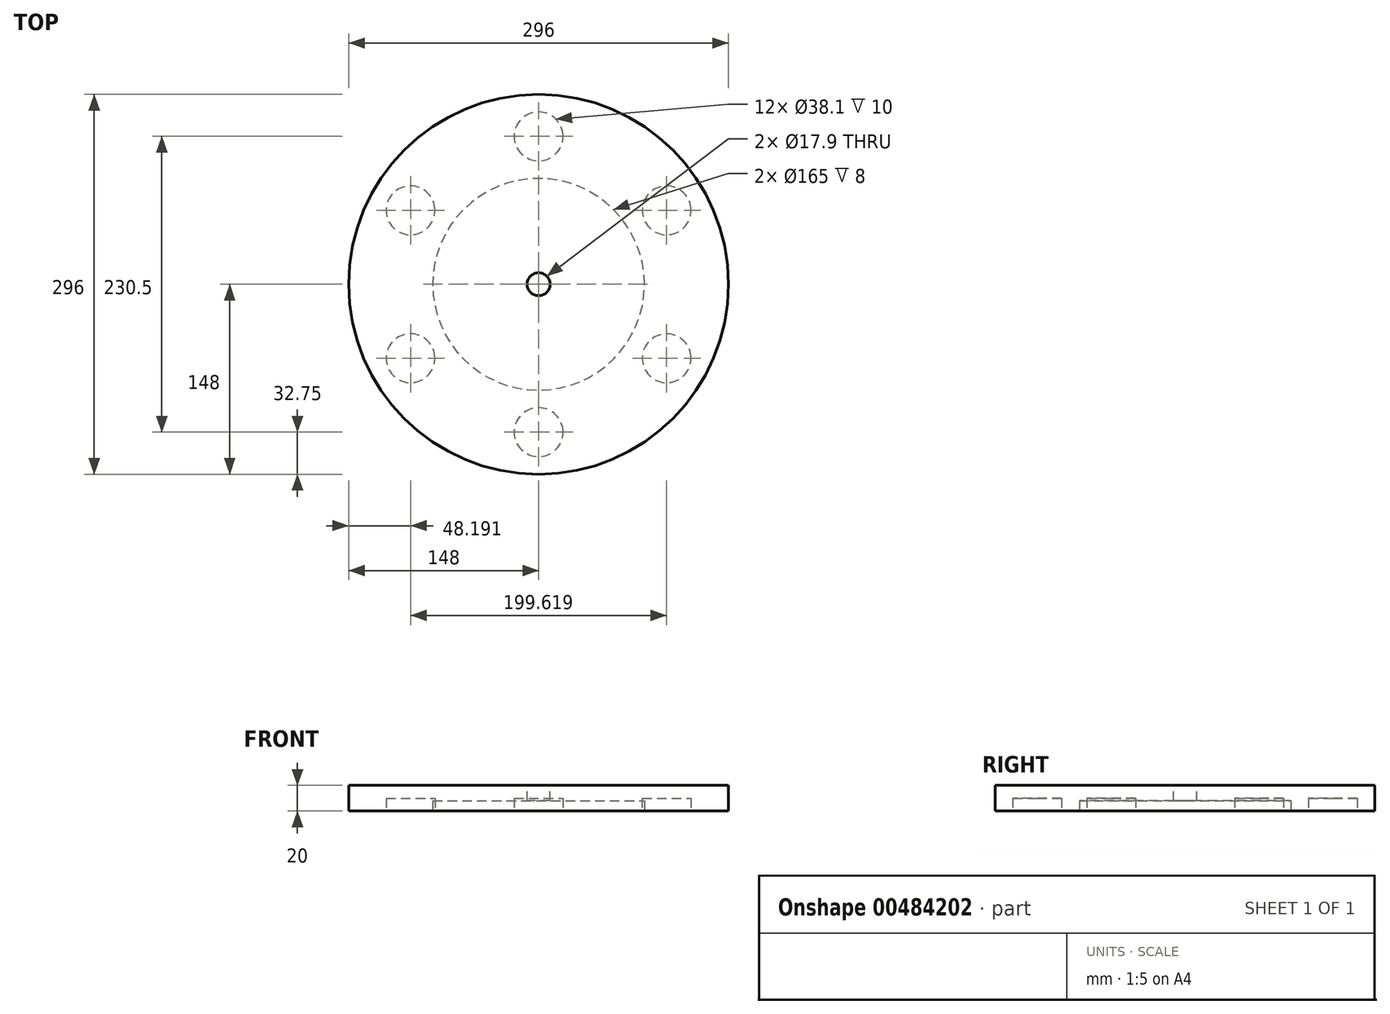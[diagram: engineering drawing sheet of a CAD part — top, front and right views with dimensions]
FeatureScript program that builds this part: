
annotation { "Feature Type Name" : "Feature", "Feature Type Description" : "" }
export const myFeature = defineFeature(function(context is Context, id is Id, definition is map)
    precondition{}
    {
        {
            var Q0;
            Q0=qCreatedBy(makeId("Top.planeOp"),FACE);
            var sketch = newSketch(context, id + "F0", { "sketchPlane" : qUnion([Q0])});
            skCircle(sketch, "E0", {"center": v(0, 0) * mm, "radius": 148 * mm});
            skCircle(sketch, "E1", {"center": v(0, 0) * mm, "radius": 8.95 * mm});
            skSolve(sketch);
        }
        {
            var Q0;
            Q0=makeQuery(id+"F0.imprint","IMPRINT",FACE,{"disambiguationData":[TD([[makeQuery(id+"F0.imprint","IMPRINT",EDGE,{"derivedFrom":sQuery(id+"F0.wireOp",EDGE,"E0")}),1.0]])]});
            extrude(context, id + "F1", {"entities" : qUnion([Q0]), "oppositeDirection" : true, "depth" : 20 * mm});
        }
        {
            var Q0;
            Q0=makeQuery(id+"F1.opExtrude","CAP_FACE",FACE,{"disambiguationData":[OSD([sQuery(id+"F0.wireOp",EDGE,"E0"),sQuery(id+"F0.wireOp",EDGE,"E1")])],"isStart":false});
            var sketch = newSketch(context, id + "F2", { "sketchPlane" : qUnion([Q0])});
            skCircle(sketch, "E2", {"center": v(0, 0) * mm, "radius": 82.5 * mm});
            skLineSegment(sketch, "E3", {"start": v(-82.5, 0) * mm, "end": v(-115.25, 0) * mm, "construction": true});
            skLineSegment(sketch, "E4", {"start": v(82.5, 0) * mm, "end": v(115.25, 0) * mm, "construction": true});
            skCircle(sketch, "E5", {"center": v(0, 0) * mm, "radius": 115.25 * mm, "construction": true});
            skLineSegment(sketch, "E6", {"start": v(0, 0) * mm, "end": v(0, 115.25) * mm, "construction": true});
            skLineSegment(sketch, "E7", {"start": v(0, 0) * mm, "end": v(99.8, 57.63) * mm, "construction": true});
            skLineSegment(sketch, "E8", {"start": v(0, 0) * mm, "end": v(99.8, -57.63) * mm, "construction": true});
            skLineSegment(sketch, "E9", {"start": v(0, 0) * mm, "end": v(0, -115.25) * mm, "construction": true});
            skLineSegment(sketch, "E10", {"start": v(0, 0) * mm, "end": v(-99.8, -57.63) * mm, "construction": true});
            skLineSegment(sketch, "E11", {"start": v(0, 0) * mm, "end": v(-99.8, 57.62) * mm, "construction": true});
            skCircle(sketch, "E12", {"center": v(-99.8, -57.63) * mm, "radius": 19.05 * mm});
            skCircle(sketch, "E13", {"center": v(0, -115.25) * mm, "radius": 19.05 * mm});
            skCircle(sketch, "E14", {"center": v(99.8, -57.62) * mm, "radius": 19.05 * mm});
            skCircle(sketch, "E15", {"center": v(99.8, 57.63) * mm, "radius": 19.05 * mm});
            skCircle(sketch, "E16", {"center": v(0, 115.25) * mm, "radius": 19.05 * mm});
            skCircle(sketch, "E17", {"center": v(-99.8, 57.62) * mm, "radius": 19.05 * mm});
            skSolve(sketch);
        }
        {
            var Q0;
            Q0=makeQuery(id+"F2.imprint","IMPRINT",FACE,{"disambiguationData":[TD([[makeQuery(id+"F2.imprint","IMPRINT",EDGE,{"derivedFrom":sQuery(id+"F2.wireOp",EDGE,"E2")}),1.0]])]});
            extrude(context, id + "F3", {"entities" : qUnion([Q0]), "operationType" : NewBodyOperationType.REMOVE, "oppositeDirection" : true, "depth" : 8 * mm});
        }
        {
            var Q0;
            Q0=makeQuery(id+"F2.imprint","IMPRINT",FACE,{"disambiguationData":[TD([[makeQuery(id+"F2.imprint","IMPRINT",EDGE,{"derivedFrom":sQuery(id+"F2.wireOp",EDGE,"E17")}),1.0]])]});
            var Q1;
            Q1=makeQuery(id+"F2.imprint","IMPRINT",FACE,{"disambiguationData":[TD([[makeQuery(id+"F2.imprint","IMPRINT",EDGE,{"derivedFrom":sQuery(id+"F2.wireOp",EDGE,"E12")}),1.0]])]});
            var Q2;
            Q2=makeQuery(id+"F2.imprint","IMPRINT",FACE,{"disambiguationData":[TD([[makeQuery(id+"F2.imprint","IMPRINT",EDGE,{"derivedFrom":sQuery(id+"F2.wireOp",EDGE,"E13")}),1.0]])]});
            var Q3;
            Q3=makeQuery(id+"F2.imprint","IMPRINT",FACE,{"disambiguationData":[TD([[makeQuery(id+"F2.imprint","IMPRINT",EDGE,{"derivedFrom":sQuery(id+"F2.wireOp",EDGE,"E14")}),1.0]])]});
            var Q4;
            Q4=makeQuery(id+"F2.imprint","IMPRINT",FACE,{"disambiguationData":[TD([[makeQuery(id+"F2.imprint","IMPRINT",EDGE,{"derivedFrom":sQuery(id+"F2.wireOp",EDGE,"E15")}),1.0]])]});
            var Q5;
            Q5=makeQuery(id+"F2.imprint","IMPRINT",FACE,{"disambiguationData":[TD([[makeQuery(id+"F2.imprint","IMPRINT",EDGE,{"derivedFrom":sQuery(id+"F2.wireOp",EDGE,"E16")}),1.0]])]});
            extrude(context, id + "F4", {"entities" : qUnion([Q0, Q1, Q2, Q3, Q4, Q5]), "operationType" : NewBodyOperationType.REMOVE, "oppositeDirection" : true, "depth" : 10 * mm});
        }
        {
            var Q0;
            Q0=makeQuery(id+"F1.opExtrude","SWEPT_BODY",BODY,{"disambiguationData":[OSD([sQuery(id+"F0.wireOp",EDGE,"E0"),sQuery(id+"F0.wireOp",EDGE,"E1")])]});
            transform(context, id + "F5", {"entities" : qUnion([Q0]), "transformType" : TransformType.TRANSLATION_3D, "dx" : 0 * mm, "dy" : 0 * mm, "dz" : 0 * mm, "makeCopy" : true});
        }
    });
